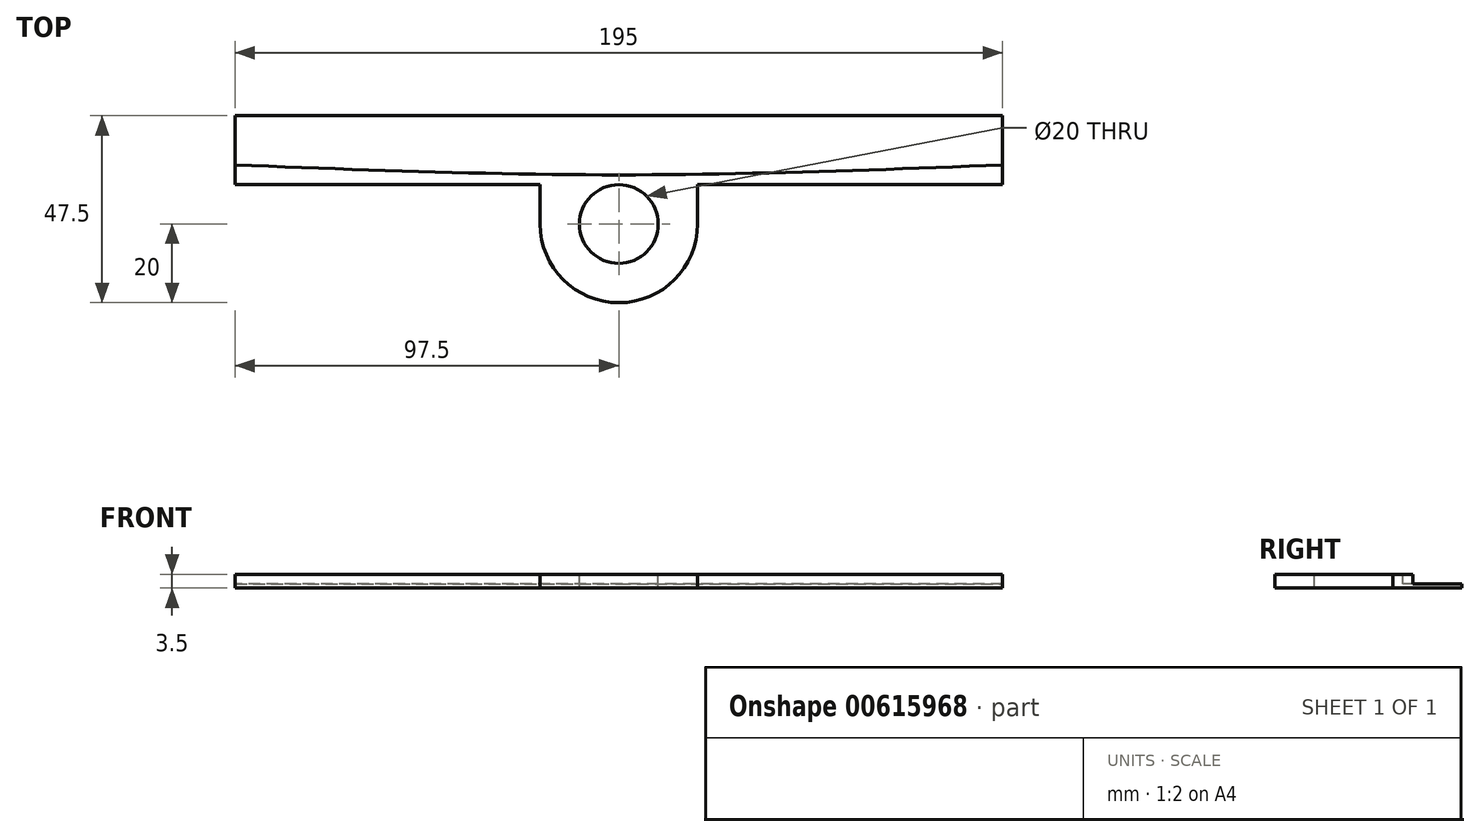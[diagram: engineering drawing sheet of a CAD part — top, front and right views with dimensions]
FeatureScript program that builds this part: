
annotation { "Feature Type Name" : "Feature", "Feature Type Description" : "" }
export const myFeature = defineFeature(function(context is Context, id is Id, definition is map)
    precondition{}
    {
        {
            var Q0;
            Q0=qCreatedBy(makeId("Top.planeOp"),FACE);
            var sketch = newSketch(context, id + "F0", { "sketchPlane" : qUnion([Q0])});
            skLineSegment(sketch, "E0.bottom", {"start": v(0, 0) * mm, "end": v(-97.5, 0) * mm});
            skLineSegment(sketch, "E0.top", {"start": v(0, 15) * mm, "end": v(-97.5, 15) * mm});
            skLineSegment(sketch, "E0.left", {"start": v(0, 0) * mm, "end": v(0, 15) * mm});
            skLineSegment(sketch, "E0.right", {"start": v(-97.5, 0) * mm, "end": v(-97.5, 15) * mm});
            skLineSegment(sketch, "E1.bottom", {"start": v(0, 0) * mm, "end": v(0, 0) * mm});
            skLineSegment(sketch, "E1.top", {"start": v(0, 29.52) * mm, "end": v(0, 29.52) * mm});
            skLineSegment(sketch, "E1.left", {"start": v(0, 0) * mm, "end": v(0, 29.52) * mm, "construction": true});
            skLineSegment(sketch, "E1.right", {"start": v(0, 0) * mm, "end": v(0, 29.52) * mm, "construction": true});
            skLineSegment(sketch, "E2.MirrorCS", {"start": v(0, 15) * mm, "end": v(97.5, 15) * mm});
            skLineSegment(sketch, "E3.MirrorCS", {"start": v(97.5, 0) * mm, "end": v(97.5, 15) * mm});
            skLineSegment(sketch, "E4.MirrorCS", {"start": v(0, 0) * mm, "end": v(97.5, 0) * mm});
            skSolve(sketch);
        }
        {
            var Q0;
            Q0=qSketchRegion(id+"F0",true);
            extrude(context, id + "F1", {"entities" : qUnion([Q0]), "depth" : 1 * mm, "offsetDistance" : 25 * mm});
        }
        {
            var Q0;
            Q0=qCreatedBy(makeId("Top.planeOp"),FACE);
            var sketch = newSketch(context, id + "F2", { "sketchPlane" : qUnion([Q0])});
            skLineSegment(sketch, "E5", {"start": v(0, 0) * mm, "end": v(20, 0) * mm});
            skLineSegment(sketch, "E6", {"start": v(20, 0) * mm, "end": v(20, -12.5) * mm});
            skLineSegment(sketch, "E7", {"start": v(20, -12.5) * mm, "end": v(-20, -12.5) * mm});
            skLineSegment(sketch, "E8", {"start": v(-20, -12.5) * mm, "end": v(-20, 0) * mm});
            skLineSegment(sketch, "E9", {"start": v(-20, 0) * mm, "end": v(0, 0) * mm});
            skCircle(sketch, "E10", {"center": v(0, -12.5) * mm, "radius": 20 * mm});
            skLineSegment(sketch, "E11", {"start": v(0, 0) * mm, "end": v(97.5, 0) * mm});
            skLineSegment(sketch, "E12", {"start": v(97.5, 0) * mm, "end": v(97.5, -2.5) * mm});
            skLineSegment(sketch, "E13", {"start": v(97.5, -2.5) * mm, "end": v(-97.5, -2.5) * mm});
            skLineSegment(sketch, "E14", {"start": v(-97.5, -2.5) * mm, "end": v(-97.5, 0) * mm});
            skLineSegment(sketch, "E15", {"start": v(-97.5, 0) * mm, "end": v(0, 0) * mm});
            skSolve(sketch);
        }
        {
            var Q0;
            {var subQ5=sQuery(id+"F2.wireOp",EDGE,"E12");Q0=makeQuery(id+"F2.imprint","IMPRINT",FACE,{"disambiguationData":[TD([[makeQuery(id+"F2.imprint","IMPRINT",EDGE,{"derivedFrom":subQ5}),-1.0]])]});}
            var Q1;
            {var subQ5=sQuery(id+"F2.wireOp",EDGE,"E14");Q1=makeQuery(id+"F2.imprint","IMPRINT",FACE,{"disambiguationData":[TD([[makeQuery(id+"F2.imprint","IMPRINT",EDGE,{"derivedFrom":subQ5}),-1.0]])]});}
            var Q2;
            {var subQ0=sQuery(id+"F2.wireOp",EDGE,"E15");var subQ1=sQuery(id+"F2.wireOp",EDGE,"E8");var subQ2=makeQuery(id+"F2.imprint","INTERSECT",VERTEX,{"derivedFrom":[subQ1,subQ0]});Q2=makeQuery(id+"F2.imprint","IMPRINT",FACE,{"disambiguationData":[TD([[makeQuery(id+"F2.imprint","IMPRINT",EDGE,{"disambiguationData":[TD([[subQ2,1.0]])],"derivedFrom":subQ1}),-1.0]])]});}
            var Q3;
            {var subQ1=sQuery(id+"F2.wireOp",EDGE,"E8");var subQ3=sQuery(id+"F2.wireOp",EDGE,"E13");var subQ4=makeQuery(id+"F2.imprint","INTERSECT",VERTEX,{"derivedFrom":[subQ1,subQ3]});Q3=makeQuery(id+"F2.imprint","IMPRINT",FACE,{"disambiguationData":[TD([[makeQuery(id+"F2.imprint","IMPRINT",EDGE,{"disambiguationData":[TD([[subQ4,1.0]])],"derivedFrom":subQ3}),1.0]])]});}
            var Q4;
            {var subQ0=sQuery(id+"F2.wireOp",EDGE,"E11");var subQ1=sQuery(id+"F2.wireOp",EDGE,"E6");var subQ2=makeQuery(id+"F2.imprint","INTERSECT",VERTEX,{"derivedFrom":[subQ1,subQ0]});Q4=makeQuery(id+"F2.imprint","IMPRINT",FACE,{"disambiguationData":[TD([[makeQuery(id+"F2.imprint","IMPRINT",EDGE,{"disambiguationData":[TD([[subQ2,-1.0]])],"derivedFrom":subQ1}),-1.0]])]});}
            var Q5;
            {var subQ1=sQuery(id+"F2.wireOp",EDGE,"E6");var subQ3=sQuery(id+"F2.wireOp",EDGE,"E13");var subQ4=makeQuery(id+"F2.imprint","INTERSECT",VERTEX,{"derivedFrom":[subQ1,subQ3]});Q5=makeQuery(id+"F2.imprint","IMPRINT",FACE,{"disambiguationData":[TD([[makeQuery(id+"F2.imprint","IMPRINT",EDGE,{"disambiguationData":[TD([[subQ4,-1.0]])],"derivedFrom":subQ3}),1.0]])]});}
            var Q6;
            Q6=sQuery(id+"F2.wireOp",EDGE,"E13");
            var Q7;
            Q7=sQuery(id+"F2.wireOp",EDGE,"E15");
            var Q8;
            Q8=sQuery(id+"F2.wireOp",EDGE,"E11");
            var Q9;
            Q9=sQuery(id+"F2.wireOp",EDGE,"E14");
            var Q10;
            Q10=sQuery(id+"F2.wireOp",EDGE,"E12");
            extrude(context, id + "F3", {"entities" : qUnion([Q0, Q1, Q2, Q3, Q4, Q5]), "surfaceEntities" : qUnion([Q6, Q7, Q8, Q9, Q10]), "depth" : 3.5 * mm, "offsetDistance" : 25 * mm});
        }
        {
            var Q0;
            {var subQ0=sQuery(id+"F2.wireOp",EDGE,"E10");var subQ2=sQuery(id+"F2.wireOp",EDGE,"E13");var subQ3=makeQuery(id+"F2.imprint","INTERSECT",VERTEX,{"disambiguationData":[OD(0.0)],"derivedFrom":[subQ0,subQ2]});Q0=makeQuery(id+"F2.imprint","IMPRINT",FACE,{"disambiguationData":[TD([[makeQuery(id+"F2.imprint","IMPRINT",EDGE,{"disambiguationData":[TD([[subQ3,-1.0]])],"derivedFrom":subQ2}),-1.0]])]});}
            var Q1;
            {var subQ0=sQuery(id+"F2.wireOp",EDGE,"E7");Q1=makeQuery(id+"F2.imprint","IMPRINT",FACE,{"disambiguationData":[TD([[makeQuery(id+"F2.imprint","IMPRINT",EDGE,{"derivedFrom":subQ0}),-1.0]])]});}
            var Q2;
            {var subQ0=sQuery(id+"F2.wireOp",EDGE,"E7");Q2=makeQuery(id+"F2.imprint","IMPRINT",FACE,{"disambiguationData":[TD([[makeQuery(id+"F2.imprint","IMPRINT",EDGE,{"derivedFrom":subQ0}),1.0]])]});}
            extrude(context, id + "F4", {"entities" : qUnion([Q0, Q1, Q2]), "depth" : 3.5 * mm, "offsetDistance" : 25 * mm});
        }
        {
            var Q0;
            {var subQ0=sQuery(id+"F2.wireOp",EDGE,"E10");var subQ1=sQuery(id+"F2.wireOp",EDGE,"E13");Q0=makeQuery(id+"F6.opBoolean","MERGE",FACE,{"derivedFrom":[makeQuery(id+"F3.opExtrude","CAP_FACE",FACE,{"disambiguationData":[OSD([sQuery(id+"F2.wireOp",EDGE,"E6"),subQ0,sQuery(id+"F2.wireOp",EDGE,"E11"),sQuery(id+"F2.wireOp",EDGE,"E12"),subQ1])],"isStart":false}),makeQuery(id+"F3.opExtrude","CAP_FACE",FACE,{"disambiguationData":[OSD([sQuery(id+"F2.wireOp",EDGE,"E8"),subQ0,subQ1,sQuery(id+"F2.wireOp",EDGE,"E14"),sQuery(id+"F2.wireOp",EDGE,"E15")])],"isStart":false}),makeQuery(id+"F4.opExtrude","CAP_FACE",FACE,{"disambiguationData":[OSD([subQ0])],"isStart":false})]});}
            var sketch = newSketch(context, id + "F5", { "sketchPlane" : qUnion([Q0])});
            skCircle(sketch, "E16", {"center": v(0, -12.5) * mm, "radius": 10 * mm});
            skSolve(sketch);
        }
        {
            var Q0;
            Q0=makeQuery(id+"F1.opExtrude","SWEPT_BODY",BODY,{"disambiguationData":[OSD([sQuery(id+"F0.wireOp",EDGE,"E0.bottom"),sQuery(id+"F0.wireOp",EDGE,"E0.top"),sQuery(id+"F0.wireOp",EDGE,"E0.right"),sQuery(id+"F0.wireOp",EDGE,"E2.MirrorCS"),sQuery(id+"F0.wireOp",EDGE,"E3.MirrorCS"),sQuery(id+"F0.wireOp",EDGE,"E4.MirrorCS")])]});
            var Q1;
            Q1=makeQuery(id+"F3.opExtrude","SWEPT_BODY",BODY,{"disambiguationData":[OSD([sQuery(id+"F2.wireOp",EDGE,"E8"),sQuery(id+"F2.wireOp",EDGE,"E10"),sQuery(id+"F2.wireOp",EDGE,"E13"),sQuery(id+"F2.wireOp",EDGE,"E14"),sQuery(id+"F2.wireOp",EDGE,"E15")])]});
            var Q2;
            Q2=makeQuery(id+"F3.opExtrude","SWEPT_BODY",BODY,{"disambiguationData":[OSD([sQuery(id+"F2.wireOp",EDGE,"E6"),sQuery(id+"F2.wireOp",EDGE,"E10"),sQuery(id+"F2.wireOp",EDGE,"E11"),sQuery(id+"F2.wireOp",EDGE,"E12"),sQuery(id+"F2.wireOp",EDGE,"E13")])]});
            var Q3;
            Q3=makeQuery(id+"FG3LRJVBiSEZoM5_3.opExtrude","SWEPT_BODY",BODY,{"disambiguationData":[OSD([sQuery(id+"F2.wireOp",EDGE,"E10")])]});
            var Q4;
            Q4=makeQuery(id+"F4.opExtrude","SWEPT_BODY",BODY,{"disambiguationData":[OSD([sQuery(id+"F2.wireOp",EDGE,"E10")])]});
            booleanBodies(context, id + "F6", {"operationType" : BooleanOperationType.UNION, "tools" : qUnion([Q0, Q1, Q2, Q3, Q4])});
        }
        {
            var Q0;
            Q0=makeQuery(id+"F5.imprint","IMPRINT",FACE,{"disambiguationData":[TD([[makeQuery(id+"F5.imprint","IMPRINT",EDGE,{"derivedFrom":sQuery(id+"F5.wireOp",EDGE,"E16")}),1.0]])]});
            extrude(context, id + "F7", {"entities" : qUnion([Q0]), "operationType" : NewBodyOperationType.REMOVE, "oppositeDirection" : true, "depth" : 3.5 * mm, "offsetDistance" : 25 * mm});
        }
        {
            var Q0;
            {var subQ0=sQuery(id+"F2.wireOp",EDGE,"E10");var subQ1=sQuery(id+"F2.wireOp",EDGE,"E13");Q0=makeQuery(id+"F6.opBoolean","MERGE",FACE,{"derivedFrom":[makeQuery(id+"F3.opExtrude","CAP_FACE",FACE,{"disambiguationData":[OSD([sQuery(id+"F2.wireOp",EDGE,"E6"),subQ0,sQuery(id+"F2.wireOp",EDGE,"E11"),sQuery(id+"F2.wireOp",EDGE,"E12"),subQ1])],"isStart":false}),makeQuery(id+"F3.opExtrude","CAP_FACE",FACE,{"disambiguationData":[OSD([sQuery(id+"F2.wireOp",EDGE,"E8"),subQ0,subQ1,sQuery(id+"F2.wireOp",EDGE,"E14"),sQuery(id+"F2.wireOp",EDGE,"E15")])],"isStart":false}),makeQuery(id+"F4.opExtrude","CAP_FACE",FACE,{"disambiguationData":[OSD([subQ0])],"isStart":false})]});}
            var sketch = newSketch(context, id + "F8", { "sketchPlane" : qUnion([Q0])});
            skLineSegment(sketch, "E17", {"start": v(0, 0) * mm, "end": v(-97.5, 0) * mm, "construction": true});
            skLineSegment(sketch, "E18", {"start": v(-97.5, 0) * mm, "end": v(-97.5, 2.5) * mm, "construction": true});
            skLineSegment(sketch, "E19", {"start": v(-97.5, 2.5) * mm, "end": v(97.5, 2.5) * mm, "construction": true});
            skLineSegment(sketch, "E20", {"start": v(97.5, 2.5) * mm, "end": v(97.5, 0) * mm, "construction": true});
            skLineSegment(sketch, "E21", {"start": v(97.5, 0) * mm, "end": v(0, 0) * mm, "construction": true});
            skFitSpline(sketch, "E22", {"points": [v(-97.5, 2.5) * mm, v(0, 0) * mm, v(97.5, 2.5) * mm], "startDerivative": vector(195, -7.5) * mm, "endDerivative": vector(195, 7.5) * mm});
            skLineSegment(sketch, "E23", {"start": v(-97.5, 2.5) * mm, "end": v(-97.5, 0) * mm});
            skLineSegment(sketch, "E24", {"start": v(97.5, 0) * mm, "end": v(97.5, 2.5) * mm});
            skLineSegment(sketch, "E25", {"start": v(-97.5, 2.5) * mm, "end": v(97.5, 2.5) * mm});
            skLineSegment(sketch, "E26", {"start": v(-97.5, 0) * mm, "end": v(97.5, 0) * mm});
            skSolve(sketch);
        }
        {
            var Q0;
            {var subQ0=sQuery(id+"F8.wireOp",EDGE,"E25");Q0=makeQuery(id+"F8.imprint","IMPRINT",FACE,{"disambiguationData":[TD([[makeQuery(id+"F8.imprint","IMPRINT",EDGE,{"derivedFrom":subQ0}),-1.0]])]});}
            extrude(context, id + "F9", {"entities" : qUnion([Q0]), "operationType" : NewBodyOperationType.REMOVE, "oppositeDirection" : true, "depth" : 2.5 * mm, "offsetDistance" : 25 * mm});
        }
        {
            var Q0;
            {var subQ0=sQuery(id+"F8.wireOp",EDGE,"E23");Q0=makeQuery(id+"F8.imprint","IMPRINT",FACE,{"disambiguationData":[TD([[makeQuery(id+"F8.imprint","IMPRINT",EDGE,{"derivedFrom":subQ0}),1.0]])]});}
            var Q1;
            {var subQ0=sQuery(id+"F8.wireOp",EDGE,"E24");Q1=makeQuery(id+"F8.imprint","IMPRINT",FACE,{"disambiguationData":[TD([[makeQuery(id+"F8.imprint","IMPRINT",EDGE,{"derivedFrom":subQ0}),1.0]])]});}
            extrude(context, id + "F10", {"entities" : qUnion([Q0, Q1]), "operationType" : NewBodyOperationType.ADD, "oppositeDirection" : true, "depth" : 3.5 * mm, "offsetDistance" : 25 * mm});
        }
    });
